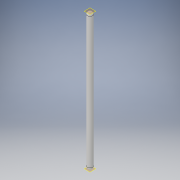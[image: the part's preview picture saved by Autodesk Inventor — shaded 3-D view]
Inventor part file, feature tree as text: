
AUTODESK INVENTOR PART (.ipt)
format: ipt  version: 2019 (Build 230136000, 136)  size: 95,744 bytes
history: native  units: in
note: dims shown in document units (in); Inventor stores cm internally (conversion verified against a paired STEP export)
features: other x1, extrude x1, fillet x1, plane x1, sketch x1
ambient origin geometry x8: Origin, YZ Plane, XZ Plane, XY Plane, X Axis, Y Axis, Z Axis, Center Point
bodies: Solid1 (feature_tree)
feature tree (5):
  other  "ball bearing replacement"
  extrude  "Extrusion1"  Depth=0.064in TaperAngle=0.0deg
  fillet  "Fillet1"  Radius=0.064in
  plane  "Work Plane1"
  sketch  "Sketch1"  dims[d0=0.128in d1=3.327in d2=0.0in d3=0.064in]
